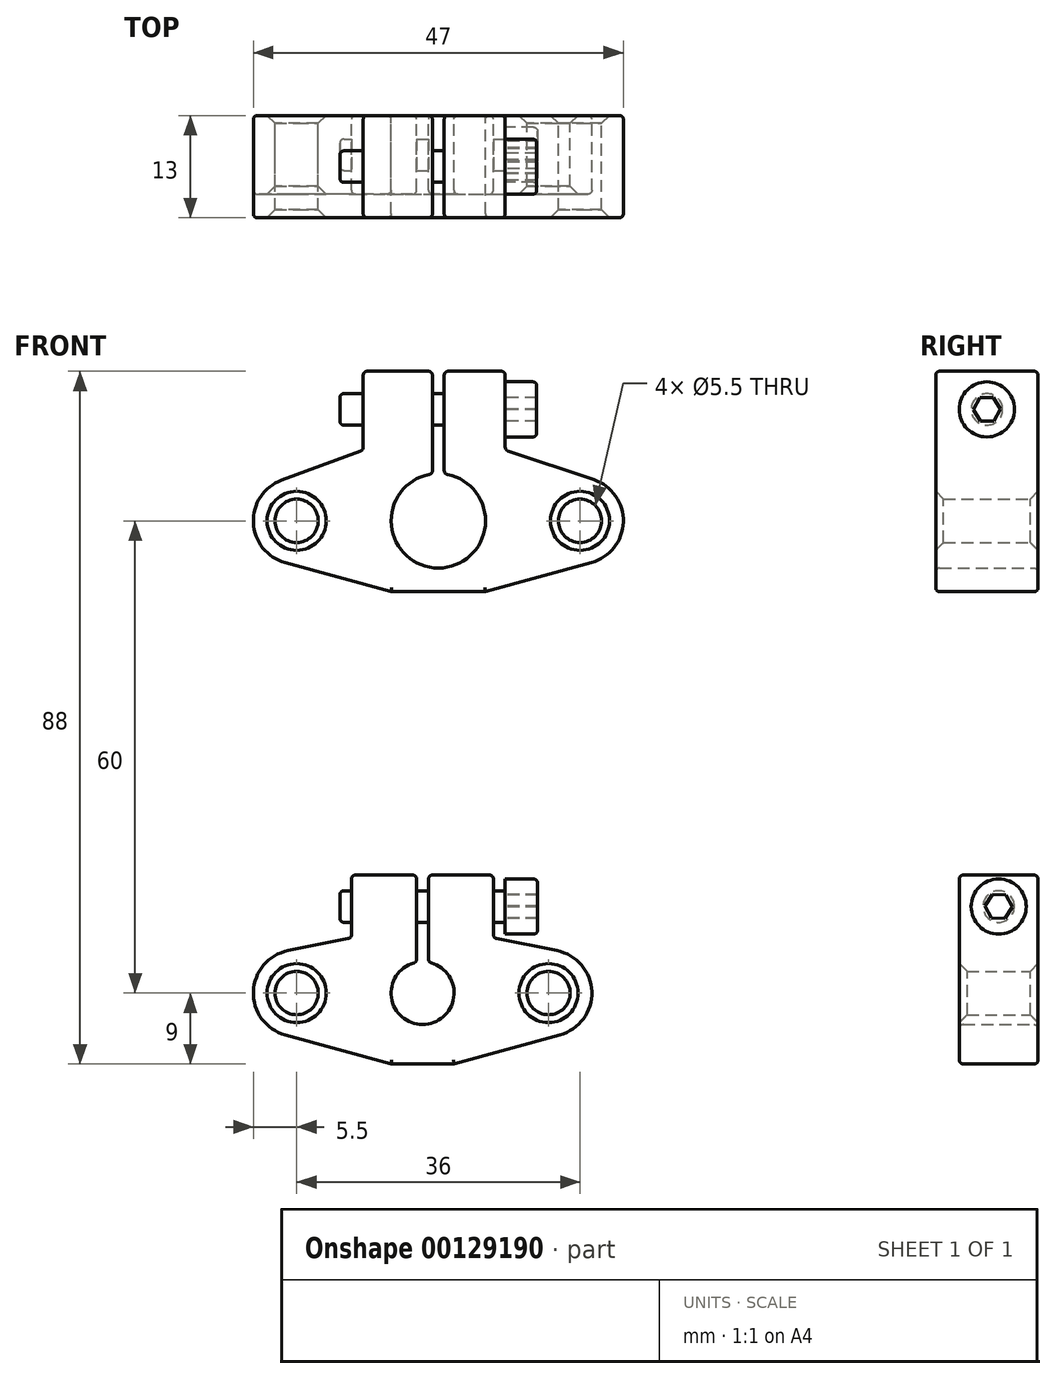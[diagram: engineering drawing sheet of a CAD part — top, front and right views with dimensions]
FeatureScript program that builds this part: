
annotation { "Feature Type Name" : "Feature", "Feature Type Description" : "" }
export const myFeature = defineFeature(function(context is Context, id is Id, definition is map)
    precondition{}
    {
        {
            var Q0;
            Q0=qCreatedBy(makeId("Right.planeOp"),FACE);
            cPlane(context, id + "F0", {"entities" : qUnion([Q0]), "cplaneType" : CPlaneType.OFFSET, "offset" : 1.5 * mm, "width" : 150 * mm, "height" : 150 * mm});
        }
        {
            var Q0;
            Q0=qCreatedBy(makeId("Front.planeOp"),FACE);
            var sketch = newSketch(context, id + "F1", { "sketchPlane" : qUnion([Q0])});
            skLineSegment(sketch, "E0", {"start": v(-33.12, -31) * mm, "end": v(22, -31) * mm, "construction": true});
            skLineSegment(sketch, "E1", {"start": v(-37.8, -40) * mm, "end": v(21.3, -40) * mm, "construction": true});
            skLineSegment(sketch, "E2", {"start": v(-40.02, -16) * mm, "end": v(22.02, -16) * mm, "construction": true});
            skCircle(sketch, "E3", {"center": v(-9, -31) * mm, "radius": 4 * mm});
            skCircle(sketch, "E4", {"center": v(-25, -31) * mm, "radius": 2.75 * mm});
            skCircle(sketch, "E5", {"center": v(7, -31) * mm, "radius": 2.75 * mm});
            skLineSegment(sketch, "E6.bottom", {"start": v(-8.25, -4.5) * mm, "end": v(-9.75, -4.5) * mm});
            skLineSegment(sketch, "E6.top", {"start": v(-8.25, -27.5) * mm, "end": v(-9.75, -27.5) * mm});
            skLineSegment(sketch, "E6.left", {"start": v(-8.25, -4.5) * mm, "end": v(-8.25, -27.5) * mm});
            skLineSegment(sketch, "E6.right", {"start": v(-9.75, -4.5) * mm, "end": v(-9.75, -27.5) * mm});
            skPoint(sketch, "E6.middle", {"position": v(-9, -16) * mm});
            skLineSegment(sketch, "E7", {"start": v(-9, 0.1) * mm, "end": v(-9, -54.19) * mm, "construction": true});
            skLineSegment(sketch, "E8.bottom", {"start": v(-18.04, -16) * mm, "end": v(0, -16) * mm});
            skLineSegment(sketch, "E8.left", {"start": v(-18.04, -16) * mm, "end": v(-18.04, -23) * mm});
            skLineSegment(sketch, "E8.right", {"start": v(0, -16) * mm, "end": v(0, -20.67) * mm});
            skLineSegment(sketch, "E9", {"start": v(-13, -40) * mm, "end": v(-5, -40) * mm});
            skLineSegment(sketch, "E10", {"start": v(-35, -24) * mm, "end": v(14.88, -24) * mm, "construction": true});
            skLineSegment(sketch, "E11", {"start": v(-18.04, -23) * mm, "end": v(-18.04, -24) * mm});
            skLineSegment(sketch, "E12", {"start": v(0, -20.67) * mm, "end": v(0, -24) * mm});
            skArc(sketch, "E13", {"start": v(-26.08, -25.6) * mm, "mid": v(-30.5, -30.8) * mm, "end": v(-26.46, -36.3) * mm});
            skArc(sketch, "E14", {"start": v(8.46, -36.3) * mm, "mid": v(12.5, -30.8) * mm, "end": v(8.07, -25.6) * mm});
            skLineSegment(sketch, "E15", {"start": v(-5, -40) * mm, "end": v(8.46, -36.3) * mm});
            skLineSegment(sketch, "E16", {"start": v(-13, -40) * mm, "end": v(-26.46, -36.3) * mm});
            skLineSegment(sketch, "E17", {"start": v(-18.04, -24) * mm, "end": v(-26.08, -25.6) * mm});
            skLineSegment(sketch, "E18", {"start": v(0, -24) * mm, "end": v(8.07, -25.6) * mm});
            skSolve(sketch);
        }
        {
            var Q0;
            Q0=makeQuery(id+"F1.imprint","IMPRINT",FACE,{"disambiguationData":[TD([[makeQuery(id+"F1.imprint","IMPRINT",EDGE,{"derivedFrom":sQuery(id+"F1.wireOp",EDGE,"E4")}),-1.0]])]});
            extrude(context, id + "F2", {"entities" : qUnion([Q0]), "depth" : 10 * mm});
        }
        {
            var Q0;
            Q0=qCreatedBy(id+"F0.planeOp",FACE);
            var sketch = newSketch(context, id + "F3", { "sketchPlane" : qUnion([Q0])});
            skLineSegment(sketch, "E19", {"start": v(-5, -17.85) * mm, "end": v(-5, -30.38) * mm, "construction": true});
            skLineSegment(sketch, "E20", {"start": v(0, -16) * mm, "end": v(-17.6, -16) * mm, "construction": true});
            skLineSegment(sketch, "E21", {"start": v(0, -24) * mm, "end": v(-18.35, -24) * mm, "construction": true});
            skLineSegment(sketch, "E22", {"start": v(-10, -13.36) * mm, "end": v(-10, -25.92) * mm, "construction": true});
            skCircle(sketch, "E23", {"center": v(-5, -20) * mm, "radius": 2 * mm});
            skCircle(sketch, "E24", {"center": v(-5, -20) * mm, "radius": 3.5 * mm});
            skLineSegment(sketch, "E25", {"start": v(-5, -20) * mm, "end": v(-18.18, -20) * mm, "construction": true});
            skCircle(sketch, "E26.cCircle", {"center": v(-5, -20) * mm, "radius": 1.5 * mm, "construction": true});
            skLineSegment(sketch, "E26.0", {"start": v(-3.27, -20.07) * mm, "end": v(-4.2, -21.53) * mm});
            skLineSegment(sketch, "E26.1", {"start": v(-4.2, -21.53) * mm, "end": v(-5.92, -21.47) * mm});
            skLineSegment(sketch, "E26.2", {"start": v(-5.92, -21.47) * mm, "end": v(-6.73, -19.93) * mm});
            skLineSegment(sketch, "E26.3", {"start": v(-6.73, -19.93) * mm, "end": v(-5.8, -18.47) * mm});
            skLineSegment(sketch, "E26.4", {"start": v(-5.8, -18.47) * mm, "end": v(-4.08, -18.53) * mm});
            skLineSegment(sketch, "E26.5", {"start": v(-4.08, -18.53) * mm, "end": v(-3.27, -20.07) * mm});
            skPoint(sketch, "E26.0.midPoint", {"position": v(-3.73, -20.8) * mm});
            skSolve(sketch);
        }
        {
            var Q0;
            Q0=makeQuery(id+"F3.imprint","IMPRINT",FACE,{"disambiguationData":[TD([[makeQuery(id+"F3.imprint","IMPRINT",EDGE,{"derivedFrom":sQuery(id+"F3.wireOp",EDGE,"E23")}),1.0]])]});
            var Q1;
            Q1=makeQuery(id+"F3.imprint","IMPRINT",FACE,{"disambiguationData":[TD([[makeQuery(id+"F3.imprint","IMPRINT",EDGE,{"derivedFrom":sQuery(id+"F3.wireOp",EDGE,"5942b489-aa47-409f-a1b6-9fd19af8fab7.0")}),-1.0]])]});
            var Q2;
            Q2=makeQuery(id+"F3.imprint","IMPRINT",FACE,{"disambiguationData":[TD([[makeQuery(id+"F3.imprint","IMPRINT",EDGE,{"derivedFrom":sQuery(id+"F3.wireOp",EDGE,"E26.0")}),-1.0]])]});
            extrude(context, id + "F4", {"entities" : qUnion([Q0, Q1, Q2]), "operationType" : NewBodyOperationType.ADD, "oppositeDirection" : true, "depth" : 21 * mm});
        }
        {
            var Q0;
            Q0=makeQuery(id+"F3.imprint","IMPRINT",FACE,{"disambiguationData":[TD([[makeQuery(id+"F3.imprint","IMPRINT",EDGE,{"derivedFrom":sQuery(id+"F3.wireOp",EDGE,"E23")}),-1.0]])]});
            var Q1;
            Q1=makeQuery(id+"F3.imprint","IMPRINT",FACE,{"disambiguationData":[TD([[makeQuery(id+"F3.imprint","IMPRINT",EDGE,{"derivedFrom":sQuery(id+"F3.wireOp",EDGE,"E23")}),1.0]])]});
            extrude(context, id + "F5", {"entities" : qUnion([Q0, Q1]), "operationType" : NewBodyOperationType.ADD, "depth" : 4.1 * mm});
        }
        {
            var Q0;
            Q0=makeQuery(id+"F2.opExtrude","CAP_EDGE",EDGE,{"disambiguationData":[OSD([sQuery(id+"F1.wireOp",EDGE,"E5")])],"isStart":false});
            var Q1;
            Q1=makeQuery(id+"F2.opExtrude","CAP_EDGE",EDGE,{"disambiguationData":[OSD([sQuery(id+"F1.wireOp",EDGE,"E5")])],"isStart":true});
            var Q2;
            Q2=makeQuery(id+"F2.opExtrude","CAP_EDGE",EDGE,{"disambiguationData":[OSD([sQuery(id+"F1.wireOp",EDGE,"E4")])],"isStart":false});
            var Q3;
            Q3=makeQuery(id+"F2.opExtrude","CAP_EDGE",EDGE,{"disambiguationData":[OSD([sQuery(id+"F1.wireOp",EDGE,"E4")])],"isStart":true});
            chamfer(context, id + "F6", {"entities" : qUnion([Q0, Q1, Q2, Q3]), "width" : 1 * mm, "tangentPropagation" : true});
        }
        {
            var Q0;
            Q0=makeQuery(id+"F2.opExtrude","CAP_EDGE",EDGE,{"disambiguationData":[OSD([sQuery(id+"F1.wireOp",EDGE,"E17")])],"isStart":false});
            var Q1;
            Q1=makeQuery(id+"F2.opExtrude","CAP_EDGE",EDGE,{"disambiguationData":[OSD([sQuery(id+"F1.wireOp",EDGE,"E8.left"),sQuery(id+"F1.wireOp",EDGE,"E11")])],"isStart":false});
            var Q2;
            {var subQ0=sQuery(id+"F1.wireOp",EDGE,"E8.bottom");Q2=makeQuery(id+"F2.opExtrude","CAP_EDGE",EDGE,{"disambiguationData":[OSD([subQ0]),TDD([makeQuery(id+"F1.imprint","IMPRINT",EDGE,{"disambiguationData":[TD([[makeQuery(id+"F1.imprint","INTERSECT",VERTEX,{"derivedFrom":[subQ0,sQuery(id+"F1.wireOp",EDGE,"E8.left")]}),-1.0]])],"derivedFrom":subQ0})])],"isStart":false});}
            var Q3;
            Q3=makeQuery(id+"F2.opExtrude","CAP_EDGE",EDGE,{"disambiguationData":[OSD([sQuery(id+"F1.wireOp",EDGE,"E6.right")])],"isStart":false});
            var Q4;
            Q4=makeQuery(id+"F2.opExtrude","CAP_EDGE",EDGE,{"disambiguationData":[OSD([sQuery(id+"F1.wireOp",EDGE,"E6.left")])],"isStart":false});
            var Q5;
            {var subQ0=sQuery(id+"F1.wireOp",EDGE,"E8.bottom");Q5=makeQuery(id+"F2.opExtrude","CAP_EDGE",EDGE,{"disambiguationData":[OSD([subQ0]),TDD([makeQuery(id+"F1.imprint","IMPRINT",EDGE,{"disambiguationData":[TD([[makeQuery(id+"F1.imprint","INTERSECT",VERTEX,{"derivedFrom":[subQ0,sQuery(id+"F1.wireOp",EDGE,"E8.right")]}),1.0]])],"derivedFrom":subQ0})])],"isStart":false});}
            var Q6;
            Q6=makeQuery(id+"F2.opExtrude","CAP_EDGE",EDGE,{"disambiguationData":[OSD([sQuery(id+"F1.wireOp",EDGE,"E8.right"),sQuery(id+"F1.wireOp",EDGE,"E12")])],"isStart":false});
            var Q7;
            Q7=makeQuery(id+"F2.opExtrude","CAP_EDGE",EDGE,{"disambiguationData":[OSD([sQuery(id+"F1.wireOp",EDGE,"E18")])],"isStart":false});
            var Q8;
            Q8=makeQuery(id+"F2.opExtrude","CAP_EDGE",EDGE,{"disambiguationData":[OSD([sQuery(id+"F1.wireOp",EDGE,"E9")])],"isStart":false});
            var Q9;
            Q9=makeQuery(id+"F2.opExtrude","CAP_EDGE",EDGE,{"disambiguationData":[OSD([sQuery(id+"F1.wireOp",EDGE,"E16")])],"isStart":true});
            var Q10;
            Q10=makeQuery(id+"F2.opExtrude","CAP_EDGE",EDGE,{"disambiguationData":[OSD([sQuery(id+"F1.wireOp",EDGE,"E8.left"),sQuery(id+"F1.wireOp",EDGE,"E11")])],"isStart":true});
            var Q11;
            {var subQ0=sQuery(id+"F1.wireOp",EDGE,"E8.bottom");Q11=makeQuery(id+"F2.opExtrude","CAP_EDGE",EDGE,{"disambiguationData":[OSD([subQ0]),TDD([makeQuery(id+"F1.imprint","IMPRINT",EDGE,{"disambiguationData":[TD([[makeQuery(id+"F1.imprint","INTERSECT",VERTEX,{"derivedFrom":[subQ0,sQuery(id+"F1.wireOp",EDGE,"E8.left")]}),-1.0]])],"derivedFrom":subQ0})])],"isStart":true});}
            var Q12;
            Q12=makeQuery(id+"F2.opExtrude","CAP_EDGE",EDGE,{"disambiguationData":[OSD([sQuery(id+"F1.wireOp",EDGE,"E6.right")])],"isStart":true});
            var Q13;
            Q13=makeQuery(id+"F2.opExtrude","CAP_EDGE",EDGE,{"disambiguationData":[OSD([sQuery(id+"F1.wireOp",EDGE,"E6.left")])],"isStart":true});
            var Q14;
            {var subQ0=sQuery(id+"F1.wireOp",EDGE,"E8.bottom");Q14=makeQuery(id+"F2.opExtrude","CAP_EDGE",EDGE,{"disambiguationData":[OSD([subQ0]),TDD([makeQuery(id+"F1.imprint","IMPRINT",EDGE,{"disambiguationData":[TD([[makeQuery(id+"F1.imprint","INTERSECT",VERTEX,{"derivedFrom":[subQ0,sQuery(id+"F1.wireOp",EDGE,"E8.right")]}),1.0]])],"derivedFrom":subQ0})])],"isStart":true});}
            var Q15;
            Q15=makeQuery(id+"F2.opExtrude","CAP_EDGE",EDGE,{"disambiguationData":[OSD([sQuery(id+"F1.wireOp",EDGE,"E8.right"),sQuery(id+"F1.wireOp",EDGE,"E12")])],"isStart":true});
            var Q16;
            Q16=makeQuery(id+"F2.opExtrude","CAP_EDGE",EDGE,{"disambiguationData":[OSD([sQuery(id+"F1.wireOp",EDGE,"E18")])],"isStart":true});
            var Q17;
            Q17=makeQuery(id+"F2.opExtrude","CAP_EDGE",EDGE,{"disambiguationData":[OSD([sQuery(id+"F1.wireOp",EDGE,"E9")])],"isStart":true});
            var Q18;
            Q18=makeQuery(id+"F2.opExtrude","SWEPT_EDGE",EDGE,{"disambiguationData":[OSD([sQuery(id+"F1.wireOp",EDGE,"E11"),sQuery(id+"F1.wireOp",EDGE,"E17")])]});
            var Q19;
            Q19=makeQuery(id+"F2.opExtrude","SWEPT_EDGE",EDGE,{"disambiguationData":[OSD([sQuery(id+"F1.wireOp",EDGE,"E12"),sQuery(id+"F1.wireOp",EDGE,"E18")])]});
            var Q20;
            Q20=makeQuery(id+"F5.opExtrude","CAP_EDGE",EDGE,{"disambiguationData":[OSD([sQuery(id+"F3.wireOp",EDGE,"E24")])],"isStart":false});
            var Q21;
            Q21=makeQuery(id+"F4.opExtrude","CAP_FACE",FACE,{"disambiguationData":[OSD([sQuery(id+"F3.wireOp",EDGE,"E23")])],"isStart":false});
            var Q22;
            Q22=makeQuery(id+"F2.opExtrude","SWEPT_EDGE",EDGE,{"disambiguationData":[OSD([sQuery(id+"F1.wireOp",EDGE,"E6.left"),sQuery(id+"F1.wireOp",EDGE,"E8.bottom")])]});
            var Q23;
            Q23=makeQuery(id+"F2.opExtrude","SWEPT_EDGE",EDGE,{"disambiguationData":[OSD([sQuery(id+"F1.wireOp",EDGE,"E6.right"),sQuery(id+"F1.wireOp",EDGE,"E8.bottom")])]});
            var Q24;
            Q24=makeQuery(id+"F2.opExtrude","CAP_EDGE",EDGE,{"disambiguationData":[OSD([sQuery(id+"F1.wireOp",EDGE,"E3")])],"isStart":false});
            var Q25;
            Q25=makeQuery(id+"F2.opExtrude","CAP_EDGE",EDGE,{"disambiguationData":[OSD([sQuery(id+"F1.wireOp",EDGE,"E3")])],"isStart":true});
            var Q26;
            Q26=makeQuery(id+"F2.opExtrude","SWEPT_EDGE",EDGE,{"disambiguationData":[OSD([sQuery(id+"F1.wireOp",EDGE,"E8.bottom"),sQuery(id+"F1.wireOp",EDGE,"E8.left")])]});
            var Q27;
            Q27=makeQuery(id+"F2.opExtrude","SWEPT_EDGE",EDGE,{"disambiguationData":[OSD([sQuery(id+"F1.wireOp",EDGE,"E8.bottom"),sQuery(id+"F1.wireOp",EDGE,"E8.right")])]});
            var Q28;
            Q28=makeQuery(id+"F2.opExtrude","SWEPT_EDGE",EDGE,{"disambiguationData":[OSD([sQuery(id+"F1.wireOp",EDGE,"E3"),sQuery(id+"F1.wireOp",EDGE,"E6.left")])]});
            var Q29;
            Q29=makeQuery(id+"F2.opExtrude","SWEPT_EDGE",EDGE,{"disambiguationData":[OSD([sQuery(id+"F1.wireOp",EDGE,"E3"),sQuery(id+"F1.wireOp",EDGE,"E6.right")])]});
            fillet(context, id + "F7", {"entities" : qUnion([Q0, Q1, Q2, Q3, Q4, Q5, Q6, Q7, Q8, Q9, Q10, Q11, Q12, Q13, Q14, Q15, Q16, Q17, Q18, Q19, Q20, Q21, Q22, Q23, Q24, Q25, Q26, Q27, Q28, Q29]), "radius" : 0.5 * mm, "tangentPropagation" : true, "allowEdgeOverflow" : false});
        }
        {
            var Q0;
            Q0=qCreatedBy(makeId("Front.planeOp"),FACE);
            var sketch = newSketch(context, id + "F8", { "sketchPlane" : qUnion([Q0])});
            skLineSegment(sketch, "E27", {"start": v(-31.62, 29) * mm, "end": v(23.5, 29) * mm, "construction": true});
            skLineSegment(sketch, "E28", {"start": v(-36.3, 20) * mm, "end": v(22.8, 20) * mm, "construction": true});
            skLineSegment(sketch, "E29", {"start": v(-37.52, 48) * mm, "end": v(23.52, 48) * mm, "construction": true});
            skCircle(sketch, "E30", {"center": v(-7, 29) * mm, "radius": 6 * mm});
            skCircle(sketch, "E31", {"center": v(-25, 29) * mm, "radius": 2.75 * mm});
            skCircle(sketch, "E32", {"center": v(11, 29) * mm, "radius": 2.75 * mm});
            skLineSegment(sketch, "E33.bottom", {"start": v(-6.25, 67) * mm, "end": v(-7.75, 67) * mm});
            skLineSegment(sketch, "E33.top", {"start": v(-6.25, 29) * mm, "end": v(-7.75, 29) * mm});
            skLineSegment(sketch, "E33.left", {"start": v(-6.25, 67) * mm, "end": v(-6.25, 29) * mm});
            skLineSegment(sketch, "E33.right", {"start": v(-7.75, 67) * mm, "end": v(-7.75, 29) * mm});
            skPoint(sketch, "E33.middle", {"position": v(-7, 48) * mm});
            skLineSegment(sketch, "E34", {"start": v(-7, 60.1) * mm, "end": v(-7, 5.81) * mm, "construction": true});
            skLineSegment(sketch, "E35.bottom", {"start": v(-16.54, 48) * mm, "end": v(1.5, 48) * mm});
            skLineSegment(sketch, "E35.left", {"start": v(-16.54, 48) * mm, "end": v(-16.54, 39) * mm});
            skLineSegment(sketch, "E35.right", {"start": v(1.5, 48) * mm, "end": v(1.5, 41.33) * mm});
            skLineSegment(sketch, "E36", {"start": v(-13, 20) * mm, "end": v(-1, 20) * mm});
            skLineSegment(sketch, "E37", {"start": v(-33.5, 38) * mm, "end": v(16.38, 38) * mm, "construction": true});
            skLineSegment(sketch, "E38", {"start": v(-16.54, 39) * mm, "end": v(-16.54, 38) * mm});
            skLineSegment(sketch, "E39", {"start": v(1.5, 41.33) * mm, "end": v(1.5, 38) * mm});
            skArc(sketch, "E40", {"start": v(-26.91, 34.16) * mm, "mid": v(-30.5, 28.76) * mm, "end": v(-26.46, 23.7) * mm});
            skArc(sketch, "E41", {"start": v(12.46, 23.7) * mm, "mid": v(16.5, 28.84) * mm, "end": v(12.75, 34.21) * mm});
            skLineSegment(sketch, "E42", {"start": v(-1, 20) * mm, "end": v(12.46, 23.7) * mm});
            skLineSegment(sketch, "E43", {"start": v(-13, 20) * mm, "end": v(-26.46, 23.7) * mm});
            skLineSegment(sketch, "E44", {"start": v(-16.54, 38) * mm, "end": v(-26.91, 34.16) * mm});
            skLineSegment(sketch, "E45", {"start": v(1.5, 38) * mm, "end": v(12.75, 34.21) * mm});
            skSolve(sketch);
        }
        {
            var Q0;
            Q0=makeQuery(id+"F8.imprint","IMPRINT",FACE,{"disambiguationData":[TD([[makeQuery(id+"F8.imprint","IMPRINT",EDGE,{"derivedFrom":sQuery(id+"F8.wireOp",EDGE,"E31")}),-1.0]])]});
            extrude(context, id + "F9", {"entities" : qUnion([Q0]), "depth" : 13 * mm});
        }
        {
            var Q0;
            Q0=qCreatedBy(id+"F0.planeOp",FACE);
            var sketch = newSketch(context, id + "F10", { "sketchPlane" : qUnion([Q0])});
            skLineSegment(sketch, "E46", {"start": v(-5, 42.15) * mm, "end": v(-5, 29.62) * mm, "construction": true});
            skLineSegment(sketch, "E47", {"start": v(-1.5, 47.16) * mm, "end": v(-19.1, 47.16) * mm, "construction": true});
            skLineSegment(sketch, "E48", {"start": v(-1.5, 39.16) * mm, "end": v(-19.85, 39.16) * mm, "construction": true});
            skCircle(sketch, "E49", {"center": v(-6.5, 43.16) * mm, "radius": 2 * mm});
            skCircle(sketch, "E50", {"center": v(-6.5, 43.16) * mm, "radius": 3.5 * mm});
            skLineSegment(sketch, "E51", {"start": v(-6.5, 43.16) * mm, "end": v(-19.68, 43.16) * mm, "construction": true});
            skCircle(sketch, "E52.cCircle", {"center": v(-6.5, 43.16) * mm, "radius": 1.5 * mm, "construction": true});
            skLineSegment(sketch, "E52.0", {"start": v(-4.77, 43.18) * mm, "end": v(-5.62, 41.67) * mm});
            skLineSegment(sketch, "E52.1", {"start": v(-5.62, 41.67) * mm, "end": v(-7.35, 41.65) * mm});
            skLineSegment(sketch, "E52.2", {"start": v(-7.35, 41.65) * mm, "end": v(-8.23, 43.14) * mm});
            skLineSegment(sketch, "E52.3", {"start": v(-8.23, 43.14) * mm, "end": v(-7.38, 44.65) * mm});
            skLineSegment(sketch, "E52.4", {"start": v(-7.38, 44.65) * mm, "end": v(-5.65, 44.67) * mm});
            skLineSegment(sketch, "E52.5", {"start": v(-5.65, 44.67) * mm, "end": v(-4.77, 43.18) * mm});
            skPoint(sketch, "E52.0.midPoint", {"position": v(-5.2, 42.42) * mm});
            skSolve(sketch);
        }
        {
            var Q0;
            Q0=makeQuery(id+"F10.imprint","IMPRINT",FACE,{"disambiguationData":[TD([[makeQuery(id+"F10.imprint","IMPRINT",EDGE,{"derivedFrom":sQuery(id+"F10.wireOp",EDGE,"E49")}),1.0]])]});
            var Q1;
            Q1=makeQuery(id+"F10.imprint","IMPRINT",FACE,{"disambiguationData":[TD([[makeQuery(id+"F10.imprint","IMPRINT",EDGE,{"derivedFrom":sQuery(id+"F10.wireOp",EDGE,"dc5590e4-4609-4243-9eb1-bd86ecfe9372.0")}),-1.0]])]});
            var Q2;
            Q2=makeQuery(id+"F10.imprint","IMPRINT",FACE,{"disambiguationData":[TD([[makeQuery(id+"F10.imprint","IMPRINT",EDGE,{"derivedFrom":sQuery(id+"F10.wireOp",EDGE,"E52.0")}),-1.0]])]});
            extrude(context, id + "F11", {"entities" : qUnion([Q0, Q1, Q2]), "operationType" : NewBodyOperationType.ADD, "oppositeDirection" : true, "depth" : 21 * mm});
        }
        {
            var Q0;
            Q0=makeQuery(id+"F10.imprint","IMPRINT",FACE,{"disambiguationData":[TD([[makeQuery(id+"F10.imprint","IMPRINT",EDGE,{"derivedFrom":sQuery(id+"F10.wireOp",EDGE,"E49")}),-1.0]])]});
            var Q1;
            Q1=makeQuery(id+"F10.imprint","IMPRINT",FACE,{"disambiguationData":[TD([[makeQuery(id+"F10.imprint","IMPRINT",EDGE,{"derivedFrom":sQuery(id+"F10.wireOp",EDGE,"E49")}),1.0]])]});
            extrude(context, id + "F12", {"entities" : qUnion([Q0, Q1]), "operationType" : NewBodyOperationType.ADD, "depth" : 4 * mm});
        }
        {
            var Q0;
            Q0=makeQuery(id+"F9.opExtrude","CAP_EDGE",EDGE,{"disambiguationData":[OSD([sQuery(id+"F8.wireOp",EDGE,"E31")])],"isStart":false});
            var Q1;
            Q1=makeQuery(id+"F9.opExtrude","CAP_EDGE",EDGE,{"disambiguationData":[OSD([sQuery(id+"F8.wireOp",EDGE,"E32")])],"isStart":false});
            var Q2;
            Q2=makeQuery(id+"F9.opExtrude","CAP_EDGE",EDGE,{"disambiguationData":[OSD([sQuery(id+"F8.wireOp",EDGE,"E32")])],"isStart":true});
            var Q3;
            Q3=makeQuery(id+"F9.opExtrude","CAP_EDGE",EDGE,{"disambiguationData":[OSD([sQuery(id+"F8.wireOp",EDGE,"E31")])],"isStart":true});
            chamfer(context, id + "F13", {"entities" : qUnion([Q0, Q1, Q2, Q3]), "width" : 1 * mm, "tangentPropagation" : true});
        }
        {
            var Q0;
            Q0=makeQuery(id+"F9.opExtrude","CAP_EDGE",EDGE,{"disambiguationData":[OSD([sQuery(id+"F8.wireOp",EDGE,"E30")])],"isStart":true});
            var Q1;
            Q1=makeQuery(id+"F9.opExtrude","CAP_EDGE",EDGE,{"disambiguationData":[OSD([sQuery(id+"F8.wireOp",EDGE,"E36")])],"isStart":true});
            var Q2;
            Q2=makeQuery(id+"F9.opExtrude","CAP_EDGE",EDGE,{"disambiguationData":[OSD([sQuery(id+"F8.wireOp",EDGE,"E42")])],"isStart":true});
            var Q3;
            Q3=makeQuery(id+"F9.opExtrude","CAP_EDGE",EDGE,{"disambiguationData":[OSD([sQuery(id+"F8.wireOp",EDGE,"E43")])],"isStart":true});
            var Q4;
            Q4=makeQuery(id+"F9.opExtrude","CAP_EDGE",EDGE,{"disambiguationData":[OSD([sQuery(id+"F8.wireOp",EDGE,"E35.right"),sQuery(id+"F8.wireOp",EDGE,"E39")])],"isStart":true});
            var Q5;
            Q5=makeQuery(id+"F12.opExtrude","CAP_EDGE",EDGE,{"disambiguationData":[OSD([sQuery(id+"F10.wireOp",EDGE,"E50")])],"isStart":false});
            var Q6;
            Q6=makeQuery(id+"F9.opExtrude","CAP_EDGE",EDGE,{"disambiguationData":[OSD([sQuery(id+"F8.wireOp",EDGE,"E35.left"),sQuery(id+"F8.wireOp",EDGE,"E38")])],"isStart":true});
            var Q7;
            Q7=makeQuery(id+"F9.opExtrude","CAP_EDGE",EDGE,{"disambiguationData":[OSD([sQuery(id+"F8.wireOp",EDGE,"E33.right")])],"isStart":true});
            var Q8;
            Q8=makeQuery(id+"F9.opExtrude","CAP_EDGE",EDGE,{"disambiguationData":[OSD([sQuery(id+"F8.wireOp",EDGE,"E33.left")])],"isStart":true});
            var Q9;
            {var subQ0=sQuery(id+"F8.wireOp",EDGE,"E35.bottom");Q9=makeQuery(id+"F9.opExtrude","SWEPT_FACE",FACE,{"disambiguationData":[OSD([subQ0]),TDD([makeQuery(id+"F8.imprint","IMPRINT",EDGE,{"disambiguationData":[TD([[makeQuery(id+"F8.imprint","INTERSECT",VERTEX,{"derivedFrom":[subQ0,sQuery(id+"F8.wireOp",EDGE,"E35.right")]}),1.0]])],"derivedFrom":subQ0})])]});}
            var Q10;
            {var subQ0=sQuery(id+"F8.wireOp",EDGE,"E35.bottom");Q10=makeQuery(id+"F9.opExtrude","SWEPT_FACE",FACE,{"disambiguationData":[OSD([subQ0]),TDD([makeQuery(id+"F8.imprint","IMPRINT",EDGE,{"disambiguationData":[TD([[makeQuery(id+"F8.imprint","INTERSECT",VERTEX,{"derivedFrom":[subQ0,sQuery(id+"F8.wireOp",EDGE,"E35.left")]}),-1.0]])],"derivedFrom":subQ0})])]});}
            var Q11;
            Q11=makeQuery(id+"F9.opExtrude","CAP_EDGE",EDGE,{"disambiguationData":[OSD([sQuery(id+"F8.wireOp",EDGE,"E44")])],"isStart":false});
            var Q12;
            Q12=makeQuery(id+"F9.opExtrude","CAP_EDGE",EDGE,{"disambiguationData":[OSD([sQuery(id+"F8.wireOp",EDGE,"E35.left"),sQuery(id+"F8.wireOp",EDGE,"E38")])],"isStart":false});
            var Q13;
            Q13=makeQuery(id+"F9.opExtrude","CAP_EDGE",EDGE,{"disambiguationData":[OSD([sQuery(id+"F8.wireOp",EDGE,"E36")])],"isStart":false});
            var Q14;
            Q14=makeQuery(id+"F9.opExtrude","CAP_EDGE",EDGE,{"disambiguationData":[OSD([sQuery(id+"F8.wireOp",EDGE,"E42")])],"isStart":false});
            var Q15;
            Q15=makeQuery(id+"F9.opExtrude","CAP_EDGE",EDGE,{"disambiguationData":[OSD([sQuery(id+"F8.wireOp",EDGE,"E35.right"),sQuery(id+"F8.wireOp",EDGE,"E39")])],"isStart":false});
            var Q16;
            Q16=makeQuery(id+"F11.opExtrude","CAP_EDGE",EDGE,{"disambiguationData":[OSD([sQuery(id+"F10.wireOp",EDGE,"E49")])],"isStart":false});
            var Q17;
            Q17=makeQuery(id+"F9.opExtrude","CAP_EDGE",EDGE,{"disambiguationData":[OSD([sQuery(id+"F8.wireOp",EDGE,"E33.left")])],"isStart":false});
            var Q18;
            Q18=makeQuery(id+"F9.opExtrude","CAP_EDGE",EDGE,{"disambiguationData":[OSD([sQuery(id+"F8.wireOp",EDGE,"E33.right")])],"isStart":false});
            var Q19;
            Q19=makeQuery(id+"F9.opExtrude","CAP_EDGE",EDGE,{"disambiguationData":[OSD([sQuery(id+"F8.wireOp",EDGE,"E30")])],"isStart":false});
            var Q20;
            Q20=makeQuery(id+"F9.opExtrude","SWEPT_EDGE",EDGE,{"disambiguationData":[OSD([sQuery(id+"F8.wireOp",EDGE,"E38"),sQuery(id+"F8.wireOp",EDGE,"E44")])]});
            var Q21;
            Q21=makeQuery(id+"F9.opExtrude","SWEPT_EDGE",EDGE,{"disambiguationData":[OSD([sQuery(id+"F8.wireOp",EDGE,"E39"),sQuery(id+"F8.wireOp",EDGE,"E45")])]});
            var Q22;
            Q22=makeQuery(id+"F9.opExtrude","SWEPT_EDGE",EDGE,{"disambiguationData":[OSD([sQuery(id+"F8.wireOp",EDGE,"E30"),sQuery(id+"F8.wireOp",EDGE,"E33.left")])]});
            var Q23;
            Q23=makeQuery(id+"F9.opExtrude","SWEPT_EDGE",EDGE,{"disambiguationData":[OSD([sQuery(id+"F8.wireOp",EDGE,"E30"),sQuery(id+"F8.wireOp",EDGE,"E33.right")])]});
            fillet(context, id + "F14", {"entities" : qUnion([Q0, Q1, Q2, Q3, Q4, Q5, Q6, Q7, Q8, Q9, Q10, Q11, Q12, Q13, Q14, Q15, Q16, Q17, Q18, Q19, Q20, Q21, Q22, Q23]), "radius" : 0.5 * mm, "tangentPropagation" : true, "allowEdgeOverflow" : false});
        }
    });
